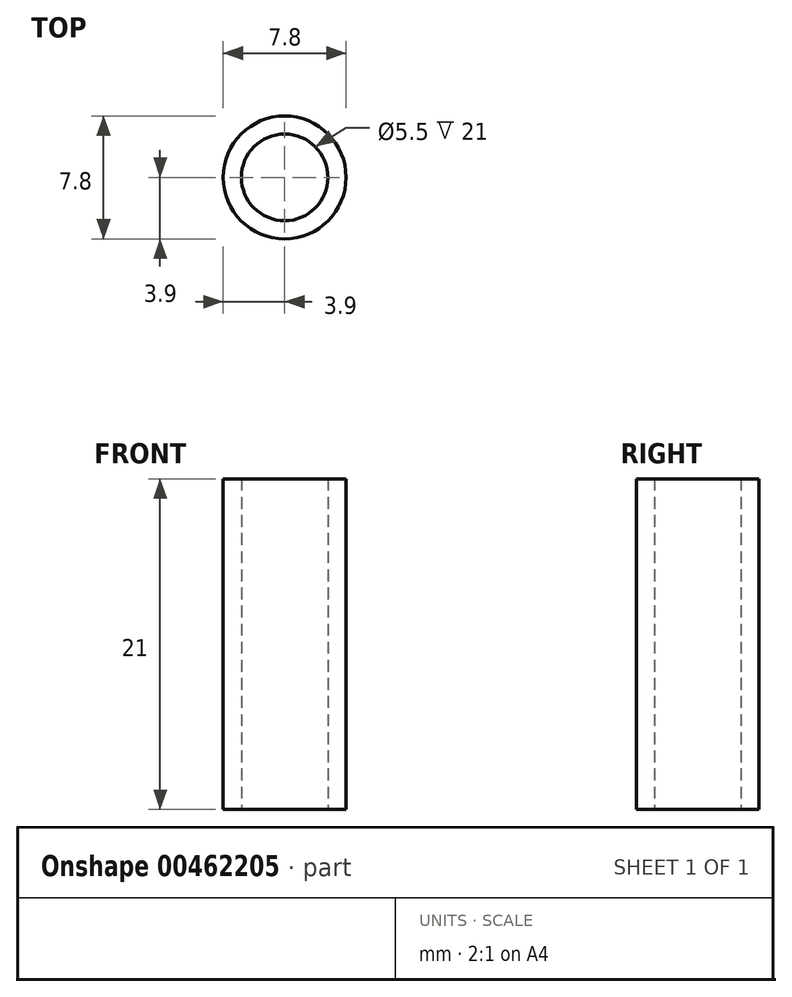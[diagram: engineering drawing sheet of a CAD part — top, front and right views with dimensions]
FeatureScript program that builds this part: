
annotation { "Feature Type Name" : "Feature", "Feature Type Description" : "" }
export const myFeature = defineFeature(function(context is Context, id is Id, definition is map)
    precondition{}
    {
        {
            var Q0;
            Q0=qCreatedBy(makeId("Top.planeOp"),FACE);
            var sketch = newSketch(context, id + "F0", { "sketchPlane" : qUnion([Q0])});
            skCircle(sketch, "E0", {"center": v(0, 0) * mm, "radius": 2.75 * mm});
            skCircle(sketch, "E1", {"center": v(0, 0) * mm, "radius": 3.9 * mm});
            skSolve(sketch);
        }
        {
            var Q0;
            Q0=makeQuery(id+"F0.imprint","IMPRINT",FACE,{"disambiguationData":[TD([[makeQuery(id+"F0.imprint","IMPRINT",EDGE,{"derivedFrom":sQuery(id+"F0.wireOp",EDGE,"E0")}),-1.0]])]});
            extrude(context, id + "F1", {"entities" : qUnion([Q0]), "depth" : 21 * mm});
        }
    });
